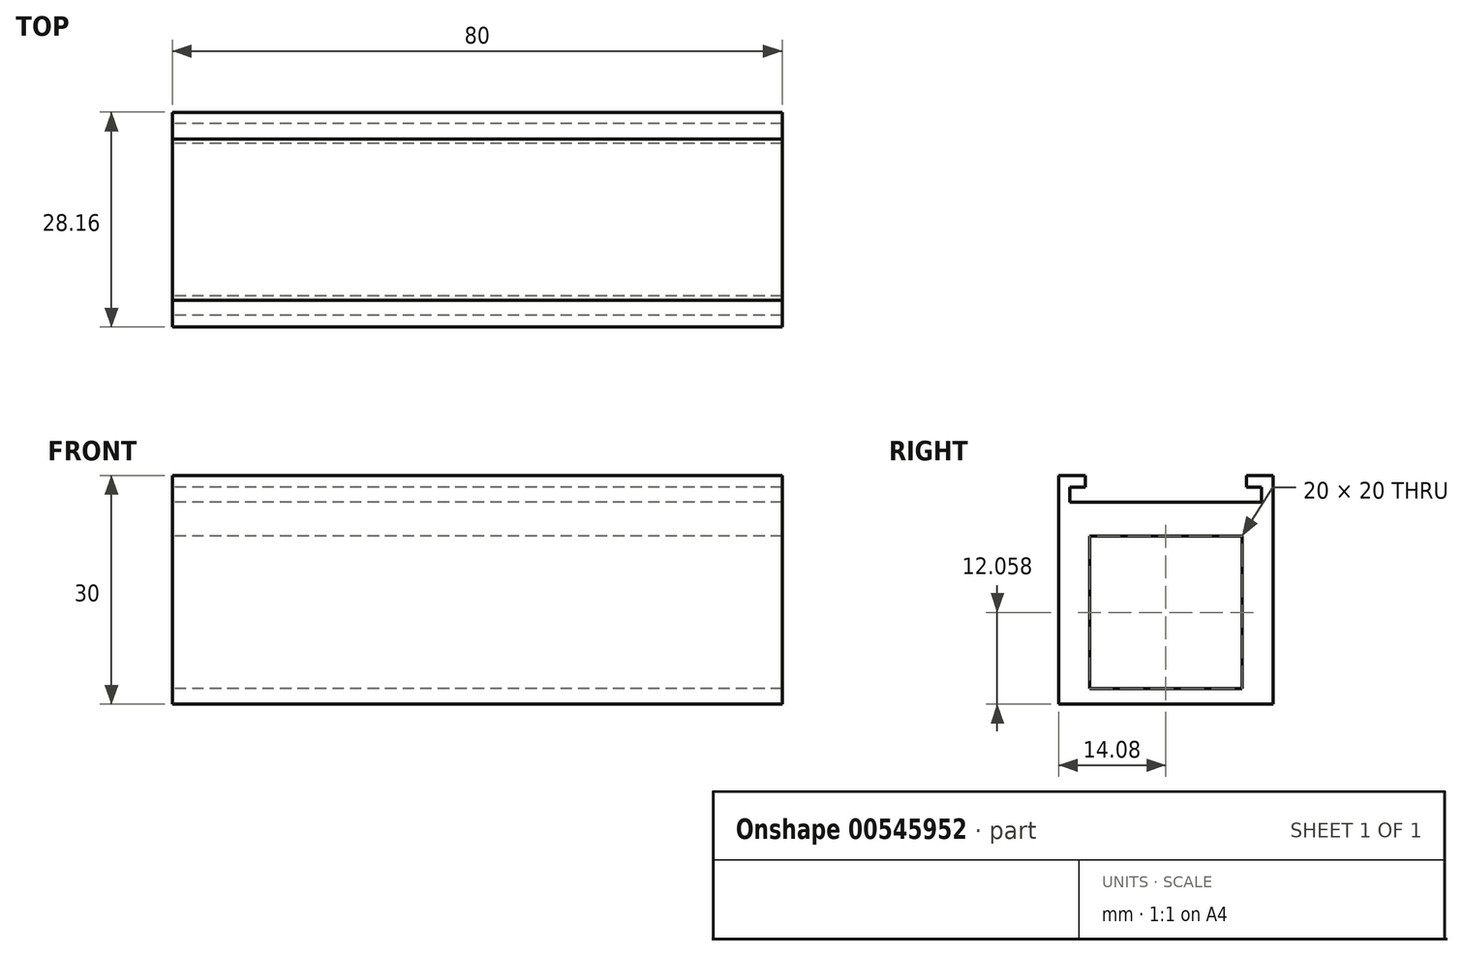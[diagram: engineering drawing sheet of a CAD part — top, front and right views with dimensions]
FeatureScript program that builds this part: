
annotation { "Feature Type Name" : "Feature", "Feature Type Description" : "" }
export const myFeature = defineFeature(function(context is Context, id is Id, definition is map)
    precondition{}
    {
        {
            var Q0;
            Q0=qCreatedBy(makeId("Right.planeOp"),FACE);
            var sketch = newSketch(context, id + "F0", { "sketchPlane" : qUnion([Q0])});
            skLineSegment(sketch, "E0", {"start": v(0, 0) * mm, "end": v(12.57, 0) * mm});
            skLineSegment(sketch, "E1", {"start": v(12.57, 0) * mm, "end": v(12.57, 2) * mm});
            skLineSegment(sketch, "E2", {"start": v(12.57, 2) * mm, "end": v(10.57, 2) * mm});
            skLineSegment(sketch, "E3", {"start": v(10.57, 2) * mm, "end": v(10.57, 3.5) * mm});
            skLineSegment(sketch, "E4", {"start": v(10.57, 3.5) * mm, "end": v(14.07, 3.5) * mm});
            skLineSegment(sketch, "E5", {"start": v(14.07, 3.5) * mm, "end": v(14.07, -26.5) * mm});
            skLineSegment(sketch, "E6", {"start": v(14.07, -26.5) * mm, "end": v(0, -26.5) * mm});
            skLineSegment(sketch, "E7.MirrorCS", {"start": v(-12.57, 2) * mm, "end": v(-10.57, 2) * mm});
            skLineSegment(sketch, "E8.MirrorCS", {"start": v(-12.57, 0) * mm, "end": v(-12.57, 2) * mm});
            skLineSegment(sketch, "E9.MirrorCS", {"start": v(-10.57, 2) * mm, "end": v(-10.57, 3.5) * mm});
            skLineSegment(sketch, "E10.MirrorCS", {"start": v(-14.07, -26.5) * mm, "end": v(0, -26.5) * mm});
            skLineSegment(sketch, "E11.MirrorCS", {"start": v(-10.57, 3.5) * mm, "end": v(-14.07, 3.5) * mm});
            skLineSegment(sketch, "E12.MirrorCS", {"start": v(0, 0) * mm, "end": v(-12.57, 0) * mm});
            skLineSegment(sketch, "E13.MirrorCS", {"start": v(-14.07, 3.5) * mm, "end": v(-14.07, -26.5) * mm});
            skLineSegment(sketch, "E14.bottom", {"start": v(-10, -4.44) * mm, "end": v(10, -4.44) * mm});
            skLineSegment(sketch, "E14.top", {"start": v(-10, -24.44) * mm, "end": v(10, -24.44) * mm});
            skLineSegment(sketch, "E14.left", {"start": v(-10, -4.44) * mm, "end": v(-10, -24.44) * mm});
            skLineSegment(sketch, "E14.right", {"start": v(10, -4.44) * mm, "end": v(10, -24.44) * mm});
            skSolve(sketch);
        }
        {
            var Q0;
            Q0=makeQuery(id+"F0.imprint","IMPRINT",FACE,{"disambiguationData":[TD([[makeQuery(id+"F0.imprint","IMPRINT",EDGE,{"derivedFrom":sQuery(id+"F0.wireOp",EDGE,"E0")}),-1.0]])]});
            extrude(context, id + "F1", {"entities" : qUnion([Q0]), "depth" : 80 * mm, "offsetDistance" : 25 * mm});
        }
    });
